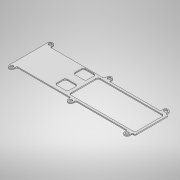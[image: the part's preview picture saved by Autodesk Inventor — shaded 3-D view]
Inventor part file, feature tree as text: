
AUTODESK INVENTOR PART (.ipt)
format: ipt  version: 2022 (Build 260153000, 153)  size: 403,968 bytes
history: native  units: mm
features: extrude x4, sketch x3, fillet x2, projected_geometry x1
ambient origin geometry x8: Origin, YZ Plane, XZ Plane, XY Plane, X Axis, Y Axis, Z Axis, Center Point
bodies: Solid1 (feature_tree)
feature tree (10):
  extrude  "Extrusion1"  Depth=30.0mm
  extrude  "Extrusion2"  Depth=1.0mm
  fillet  "Fillet2"  Radius=1.0mm
  extrude  "Extrusion5"  Depth=17.5mm
  extrude  "Extrusion15"  Depth=28.0mm
  fillet  "Fillet4"  Radius=1.0mm
  sketch  "Sketch1"  dims[d0=37.0mm d1=30.0mm]
  sketch  "Sketch2"  dims[d2=18.0mm d3=37.5mm d4=1.0mm]
  projected_geometry  "Projected Loop1"
  sketch  "Sketch5"  dims[d5=6.0mm d6=17.5mm d7=28.0mm d8=1.0mm d9=1.0mm d10=1.0mm d11=1.0mm d12=117.5mm d13=2.0mm d14=2.0mm d15=1.0mm d16=1.0mm d17=2.0mm d18=2.0mm d19=2.0mm d20=2.0mm d21=2.5mm d22=2.5mm d23=5.0mm d24=2.5mm d25=2.5mm d26=2.5mm d27=2.5mm d28=5.0mm d29=5.0mm d30=2.5mm d31=3.1mm d32=3.1mm d33=3.1mm d34=3.1mm d35=3.1mm d36=3.1mm d37=7.0mm d38=0.0mm d39=1.0mm d40=0.0mm d44=1.0mm d45=1.0mm d46=0.5mm d47=0.0mm d48=1.0mm d49=1.0mm d50=1.0mm d51=1.0mm d53=1.0mm d61=7.0mm d62=0.0mm d114=2.0mm d115=2.0mm d116=2.0mm d117=53.0mm d118=50.0mm d119=12.0mm d120=1.0mm d121=3.5mm d122=13.5mm d123=11.0mm d124=20.0mm d125=0.0mm d126=2.0mm d127=2.5mm d128=9.5mm]
